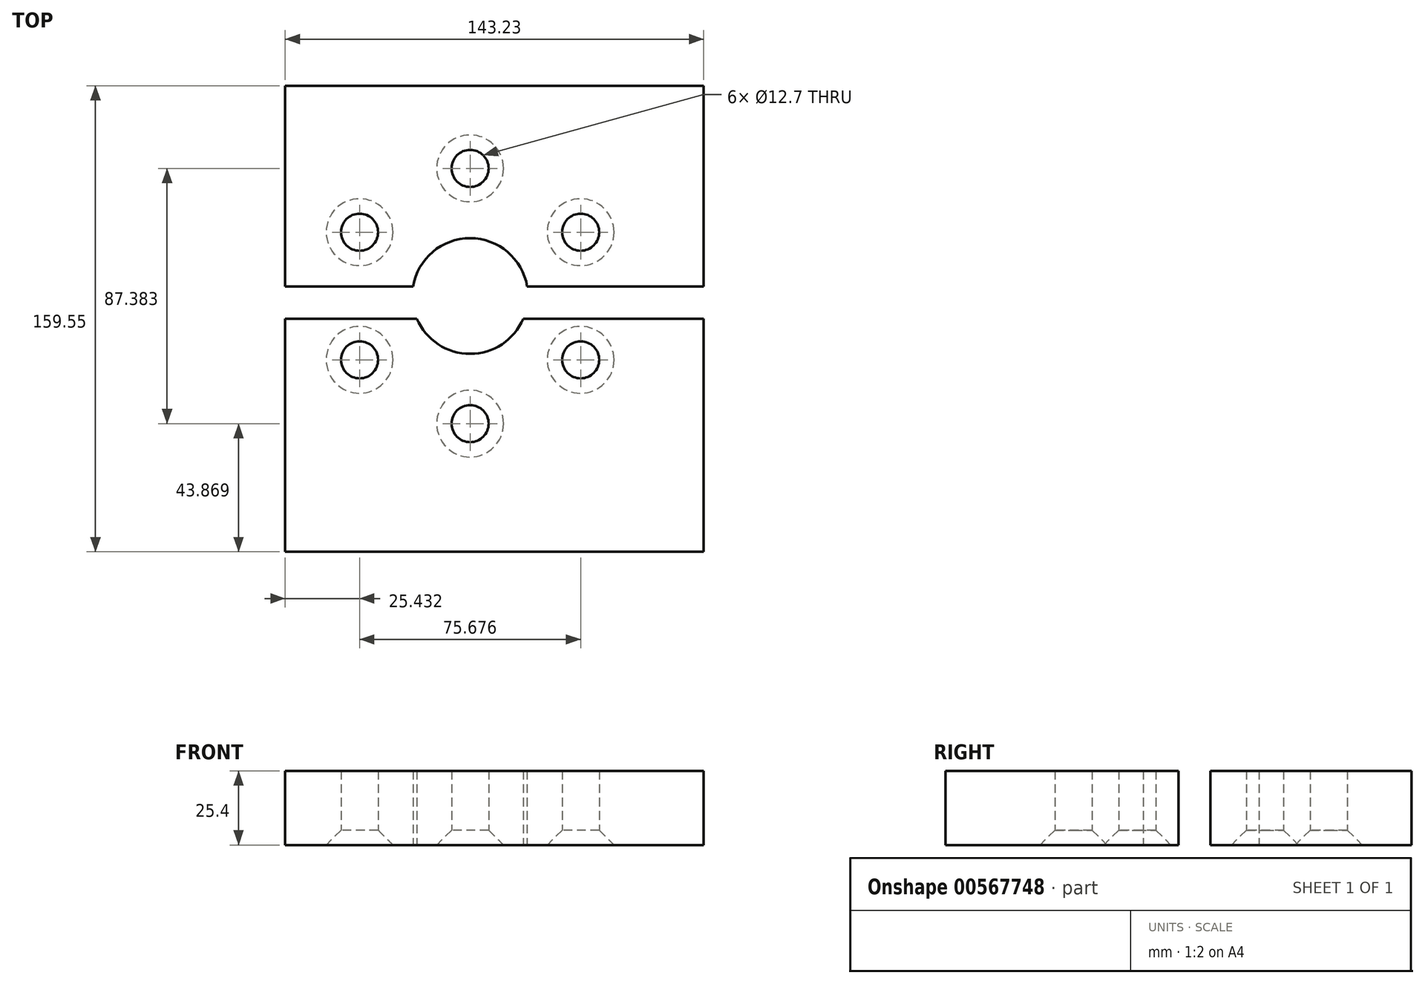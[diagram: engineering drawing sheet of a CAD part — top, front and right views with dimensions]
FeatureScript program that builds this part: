
annotation { "Feature Type Name" : "Feature", "Feature Type Description" : "" }
export const myFeature = defineFeature(function(context is Context, id is Id, definition is map)
    precondition{}
    {
        {
            var Q0;
            Q0=qCreatedBy(makeId("Top.planeOp"),FACE);
            var sketch = newSketch(context, id + "F0", { "sketchPlane" : qUnion([Q0])});
            skLineSegment(sketch, "E0.bottom", {"start": v(-63.27, 72) * mm, "end": v(79.96, 72) * mm});
            skLineSegment(sketch, "E0.top", {"start": v(-63.27, -87.56) * mm, "end": v(79.96, -87.56) * mm});
            skLineSegment(sketch, "E0.left", {"start": v(-63.27, 72) * mm, "end": v(-63.27, -87.56) * mm});
            skLineSegment(sketch, "E0.right", {"start": v(79.96, 72) * mm, "end": v(79.96, -87.56) * mm});
            skCircle(sketch, "E1", {"center": v(0, 0) * mm, "radius": 19.8 * mm});
            skCircle(sketch, "E2", {"center": v(0, 43.7) * mm, "radius": 6.35 * mm});
            skCircle(sketch, "E3.1.0", {"center": v(-37.84, 21.85) * mm, "radius": 6.35 * mm});
            skCircle(sketch, "E3.2.0", {"center": v(-37.84, -21.85) * mm, "radius": 6.35 * mm});
            skCircle(sketch, "E3.3.0", {"center": v(0, -43.7) * mm, "radius": 6.35 * mm});
            skCircle(sketch, "E3.4.0", {"center": v(37.84, -21.85) * mm, "radius": 6.35 * mm});
            skCircle(sketch, "E3.5.0", {"center": v(37.84, 21.85) * mm, "radius": 6.35 * mm});
            skSolve(sketch);
        }
        {
            var Q0;
            Q0=makeQuery(id+"F0.imprint","IMPRINT",FACE,{"disambiguationData":[TD([[makeQuery(id+"F0.imprint","IMPRINT",EDGE,{"derivedFrom":sQuery(id+"F0.wireOp",EDGE,"E0.bottom")}),-1.0]])]});
            extrude(context, id + "F1", {"entities" : qUnion([Q0]), "depth" : 25.4 * mm, "offsetDistance" : 25.4 * mm});
        }
        {
            var Q0;
            Q0=makeQuery(id+"F1.opExtrude","CAP_EDGE",EDGE,{"disambiguationData":[OSD([sQuery(id+"F0.wireOp",EDGE,"E3.3.0")])],"isStart":true});
            var Q1;
            Q1=makeQuery(id+"F1.opExtrude","CAP_EDGE",EDGE,{"disambiguationData":[OSD([sQuery(id+"F0.wireOp",EDGE,"E3.4.0")])],"isStart":true});
            var Q2;
            Q2=makeQuery(id+"F1.opExtrude","CAP_EDGE",EDGE,{"disambiguationData":[OSD([sQuery(id+"F0.wireOp",EDGE,"E3.5.0")])],"isStart":true});
            var Q3;
            Q3=makeQuery(id+"F1.opExtrude","CAP_EDGE",EDGE,{"disambiguationData":[OSD([sQuery(id+"F0.wireOp",EDGE,"E2")])],"isStart":true});
            var Q4;
            Q4=makeQuery(id+"F1.opExtrude","CAP_EDGE",EDGE,{"disambiguationData":[OSD([sQuery(id+"F0.wireOp",EDGE,"E3.1.0")])],"isStart":true});
            var Q5;
            Q5=makeQuery(id+"F1.opExtrude","CAP_EDGE",EDGE,{"disambiguationData":[OSD([sQuery(id+"F0.wireOp",EDGE,"E3.2.0")])],"isStart":true});
            chamfer(context, id + "F2", {"entities" : qUnion([Q0, Q1, Q2, Q3, Q4, Q5]), "width" : 5.08 * mm, "tangentPropagation" : true});
        }
        {
            var Q0;
            Q0=makeQuery(id+"F1.opExtrude","CAP_FACE",FACE,{"disambiguationData":[OSD([sQuery(id+"F0.wireOp",EDGE,"E0.bottom"),sQuery(id+"F0.wireOp",EDGE,"E0.top"),sQuery(id+"F0.wireOp",EDGE,"E0.left"),sQuery(id+"F0.wireOp",EDGE,"E0.right"),sQuery(id+"F0.wireOp",EDGE,"E1"),sQuery(id+"F0.wireOp",EDGE,"E2"),sQuery(id+"F0.wireOp",EDGE,"E3.1.0"),sQuery(id+"F0.wireOp",EDGE,"E3.2.0"),sQuery(id+"F0.wireOp",EDGE,"E3.3.0"),sQuery(id+"F0.wireOp",EDGE,"E3.4.0"),sQuery(id+"F0.wireOp",EDGE,"E3.5.0")])],"isStart":false});
            var sketch = newSketch(context, id + "F3", { "sketchPlane" : qUnion([Q0])});
            skLineSegment(sketch, "E4.bottom", {"start": v(-63.27, 3.23) * mm, "end": v(79.96, 3.23) * mm});
            skLineSegment(sketch, "E4.top", {"start": v(-63.27, -7.78) * mm, "end": v(79.96, -7.78) * mm});
            skLineSegment(sketch, "E4.left", {"start": v(-63.27, 3.23) * mm, "end": v(-63.27, -7.78) * mm});
            skLineSegment(sketch, "E4.right", {"start": v(79.96, 3.23) * mm, "end": v(79.96, -7.78) * mm});
            skSolve(sketch);
        }
        {
            var Q0;
            Q0 = qSketchRegion(id + "F3", true);
            extrude(context, id + "F4", {"entities" : qUnion([Q0]), "operationType" : NewBodyOperationType.REMOVE, "oppositeDirection" : true, "depth" : 25.4 * mm, "offsetDistance" : 25.4 * mm});
        }
    });
